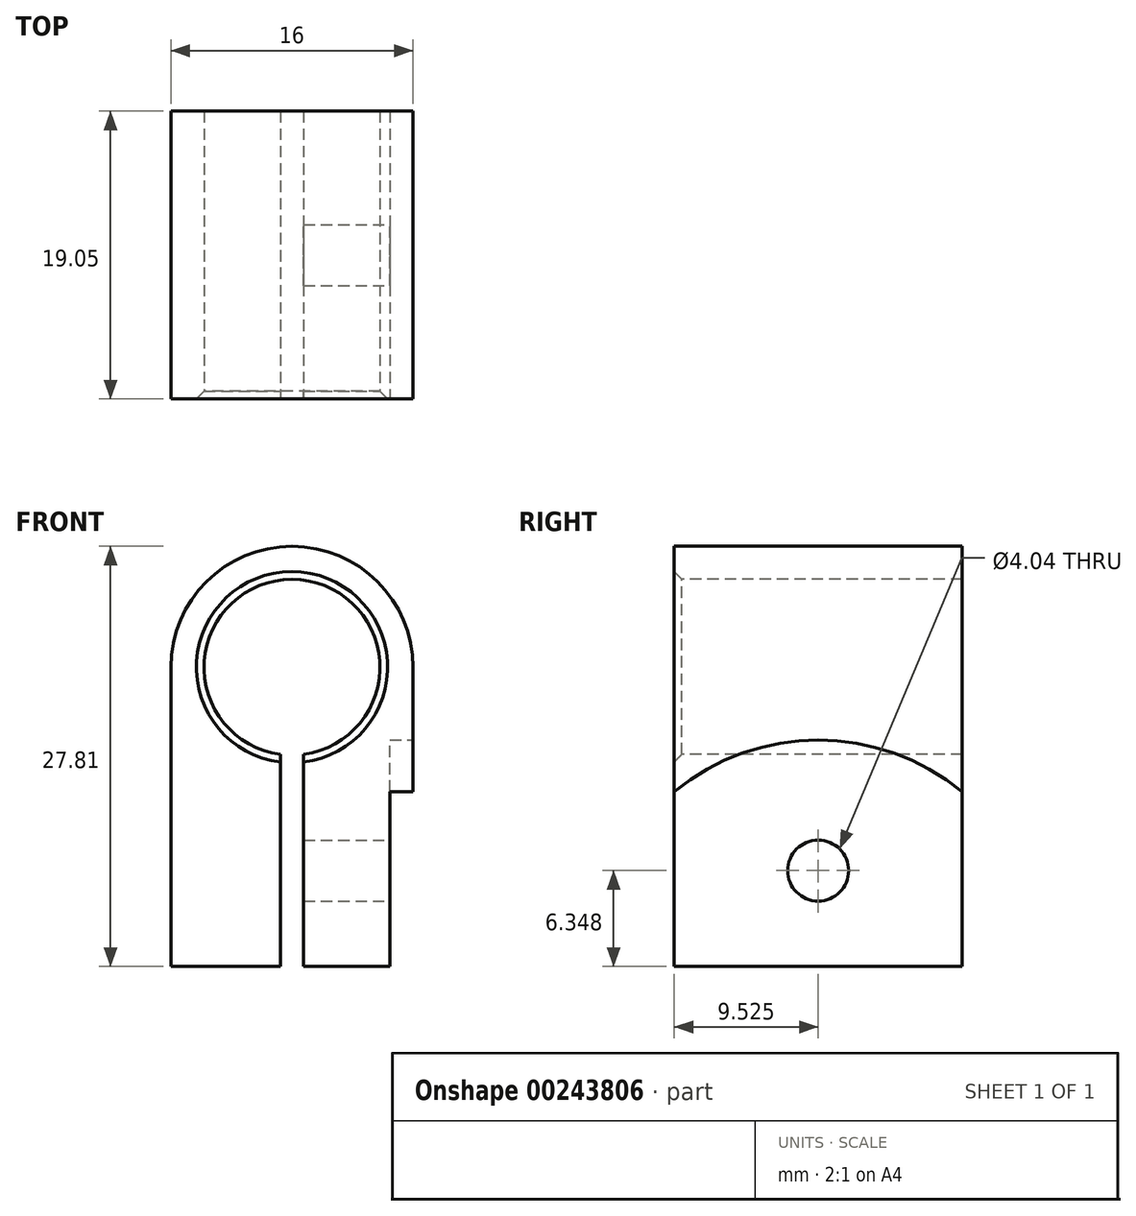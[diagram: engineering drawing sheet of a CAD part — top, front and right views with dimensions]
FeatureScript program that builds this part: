
annotation { "Feature Type Name" : "Feature", "Feature Type Description" : "" }
export const myFeature = defineFeature(function(context is Context, id is Id, definition is map)
    precondition{}
    {
        {
            var Q0;
            Q0=qCreatedBy(makeId("Front.planeOp"),FACE);
            var sketch = newSketch(context, id + "F0", { "sketchPlane" : qUnion([Q0])});
            skArc(sketch, "E0", {"start": v(8, 0) * mm, "mid": v(0, 8) * mm, "end": v(-8, 0) * mm});
            skLineSegment(sketch, "E1", {"start": v(0.76, -19.81) * mm, "end": v(0.76, -5.77) * mm});
            skLineSegment(sketch, "E2.MirrorCS", {"start": v(-0.76, -19.81) * mm, "end": v(-0.76, -5.77) * mm});
            skLineSegment(sketch, "E3", {"start": v(0.76, -19.81) * mm, "end": v(8, -19.81) * mm});
            skPoint(sketch, "E3.endSnap0", {"position": v(0.38, -19.81) * mm});
            skLineSegment(sketch, "E4", {"start": v(8, -19.81) * mm, "end": v(8, 0) * mm});
            skLineSegment(sketch, "E5", {"start": v(-0.76, -19.81) * mm, "end": v(-8, -19.81) * mm});
            skLineSegment(sketch, "E6", {"start": v(-8, -19.81) * mm, "end": v(-8, 0) * mm});
            skArc(sketch, "E7", {"start": v(0.76, -5.77) * mm, "mid": v(0, 5.82) * mm, "end": v(-0.76, -5.77) * mm});
            skPoint(sketch, "E8.orphan", {"position": v(0.76, -6.07) * mm});
            skPoint(sketch, "E9.orphan", {"position": v(-0.76, -6.07) * mm});
            skPoint(sketch, "E10.orphan", {"position": v(0, -19.81) * mm});
            skSolve(sketch);
        }
        {
            var Q0;
            Q0 = qSketchRegion(id + "F0", true);
            extrude(context, id + "F1", {"entities" : qUnion([Q0]), "oppositeDirection" : true, "depth" : 19.05 * mm});
        }
        {
            var Q0;
            Q0=makeQuery(id+"F1.opExtrude","CAP_EDGE",EDGE,{"disambiguationData":[OSD([sQuery(id+"F0.wireOp",EDGE,"E7")])],"isStart":true});
            chamfer(context, id + "F2", {"entities" : qUnion([Q0]), "width" : 0.5 * mm, "tangentPropagation" : true});
        }
        {
            var Q0;
            Q0=makeQuery(id+"F1.opExtrude","SWEPT_FACE",FACE,{"disambiguationData":[OSD([sQuery(id+"F0.wireOp",EDGE,"E4")])]});
            var sketch = newSketch(context, id + "F3", { "sketchPlane" : qUnion([Q0])});
            skArc(sketch, "E11", {"start": v(19.05, -8.24) * mm, "mid": v(9.52, -4.83) * mm, "end": v(0, -8.24) * mm});
            skLineSegment(sketch, "E12.0", {"start": v(19.05, -19.81) * mm, "end": v(0, -19.81) * mm});
            skLineSegment(sketch, "E12.1", {"start": v(0, -19.81) * mm, "end": v(0, -8.24) * mm});
            skLineSegment(sketch, "E12.2", {"start": v(19.05, -19.81) * mm, "end": v(19.05, -8.24) * mm});
            skPoint(sketch, "E13.orphan", {"position": v(0, 0) * mm});
            skPoint(sketch, "E14.orphan", {"position": v(19.05, 0) * mm});
            skSolve(sketch);
        }
        {
            var Q0;
            Q0 = qSketchRegion(id + "F3", true);
            extrude(context, id + "F4", {"entities" : qUnion([Q0]), "operationType" : NewBodyOperationType.REMOVE, "oppositeDirection" : true, "depth" : 1.52 * mm});
        }
        {
            var Q0;
            Q0=makeQuery(id+"F4.boolean.opBoolean","COPY",FACE,{"derivedFrom":makeQuery(id+"F4.opExtrude","CAP_FACE",FACE,{"disambiguationData":[OSD([sQuery(id+"F3.wireOp",EDGE,"E11"),sQuery(id+"F3.wireOp",EDGE,"E12.0"),sQuery(id+"F3.wireOp",EDGE,"E12.1"),sQuery(id+"F3.wireOp",EDGE,"E12.2")])],"isStart":false})});
            var sketch = newSketch(context, id + "F5", { "sketchPlane" : qUnion([Q0])});
            skPoint(sketch, "E15", {"position": v(9.53, -13.46) * mm});
            skSolve(sketch);
        }
        {
            var Q0;
            Q0=sQuery(id+"F5.wireOp",VERTEX,"E15");
            var Q1;
            Q1=makeQuery(id+"F1.opExtrude","SWEPT_BODY",BODY,{"disambiguationData":[OSD([sQuery(id+"F0.wireOp",EDGE,"E0"),sQuery(id+"F0.wireOp",EDGE,"E1"),sQuery(id+"F0.wireOp",EDGE,"E2.MirrorCS"),sQuery(id+"F0.wireOp",EDGE,"E3"),sQuery(id+"F0.wireOp",EDGE,"E4"),sQuery(id+"F0.wireOp",EDGE,"E5"),sQuery(id+"F0.wireOp",EDGE,"E6"),sQuery(id+"F0.wireOp",EDGE,"E7")])]});
            hole(context, id + "F6", {"style" : HoleStyle.SIMPLE, "endStyle" : HoleEndStyle.BLIND, "standardTappedOrClearance" : lookupTablePath({ "standard" : "ANSI", "engagement" : "75%", "pitch" : "32 tpi", "size" : "#10", "type" : "Tapped" }), "standardBlindInLast" : lookupTablePath({ "standard" : "ANSI", "engagement" : "75%", "pitch" : "32 tpi", "size" : "#10", "type" : "Tapped" }), "holeDiameter" : 4.04 * mm, "holeDepth" : 5.84 * mm, "startFromSketch" : true, "locations" : qUnion([Q0]), "scope" : qUnion([Q1]), "majorDiameter" : 4.83 * mm});
        }
    });
